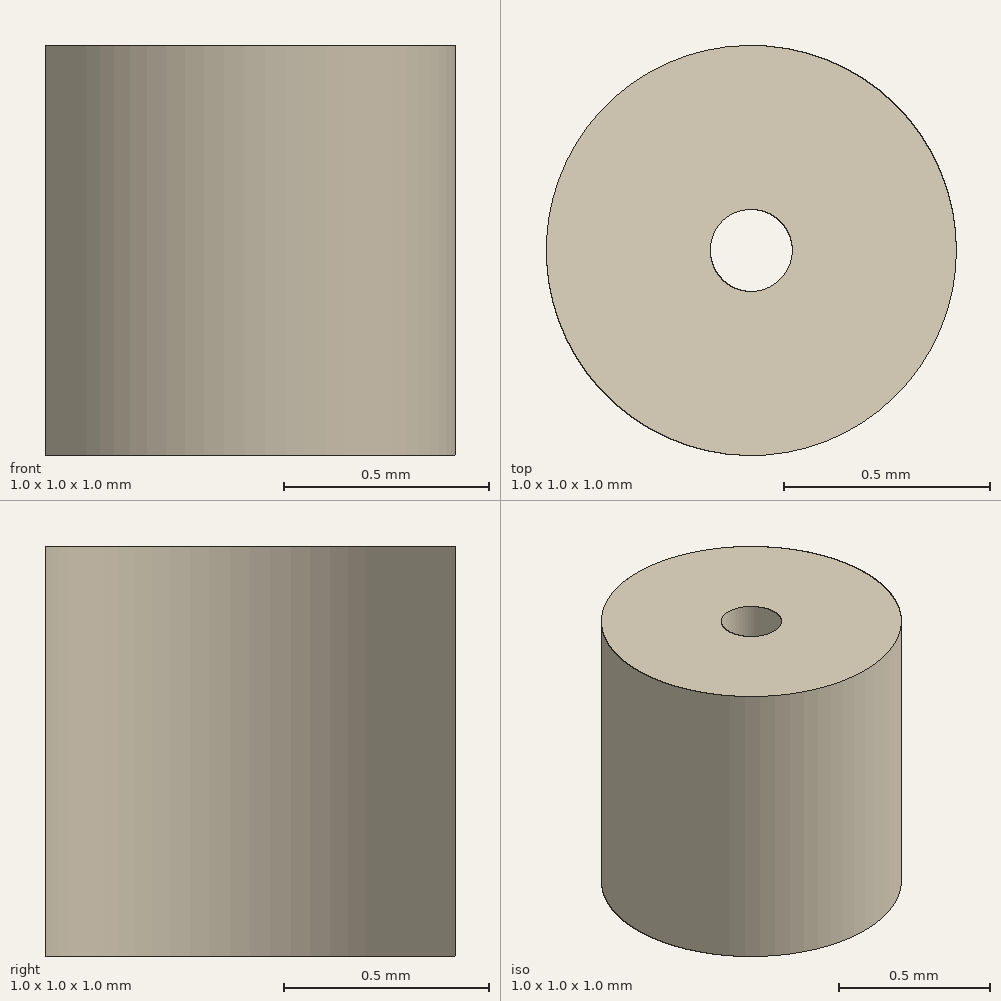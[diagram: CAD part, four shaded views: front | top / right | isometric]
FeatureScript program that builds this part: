
annotation { "Feature Type Name" : "Feature", "Feature Type Description" : "" }
export const myFeature = defineFeature(function(context is Context, id is Id, definition is map)
    precondition{}
    {
        {
            var Q0;
            Q0=qCreatedBy(makeId("Top.planeOp"),FACE);
            var sketch = newSketch(context, id + "F0", { "sketchPlane" : qUnion([Q0])});
            skCircle(sketch, "E0", {"center": v(0, 0) * mm, "radius": 0.5 * mm});
            skCircle(sketch, "E1", {"center": v(0, 0) * mm, "radius": 0.1 * mm});
            skSolve(sketch);
        }
        {
            var Q0;
            Q0=makeQuery(id+"F0.imprint","IMPRINT",FACE,{"disambiguationData":[TD([[makeQuery(id+"F0.imprint","IMPRINT",EDGE,{"derivedFrom":sQuery(id+"F0.wireOp",EDGE,"E0")}),1.0]])]});
            extrude(context, id + "F1", {"entities" : qUnion([Q0]), "depth" : 1 * mm});
        }
    });
